# Revit family: Accessory-Drying_Rack-KOHLER-Ledge-K-35006
name_source: partatom
category: Specialty Equipment
units: mm (PartAtom-declared; Revit-internal decimal feet)

## family parameters
Cut with Voids When Loaded = No
Host = Face
OmniClass Number = 23.31.25.00
Part Type = Normal
Room Calculation Point = No
Round Connector Dimension = Use Diameter
Shared = No

## types (1)
- NA-Not Applicable
    ADA Compliant = No
    Assembly Code = C1030200
    Date Modified = 05/14/2024
    Default Elevation = 42"
    Description = Drying Rack
    Finish = KOHLER-Metal-ST-Stainless_Steel
    Height = 7/16"
    Length = 16 5/16"
    Manufacturer = Kohler Co.
    Master Format 2014 = 10 28 00
    Master Format 2014 Name = Toilet, Bath, and Laundry Accessories
    Material = Premium Metal Construction
    Model = K-35006-NA
    Product Documentation Link = https://www.us.kohler.com
    Product Name = Ledge
    Product Page URL = http://www.us.kohler.com
    Secondary Finish = Plastic-Pantone-Gray_2332C
    Type = 1
    URL = https://www.us.kohler.com
    WaterSense Certified = No
    Width = 11 15/16"

## geometry (parser evidence)
native form markers: Sweep x6
no freeform markers — native parametric forms only
